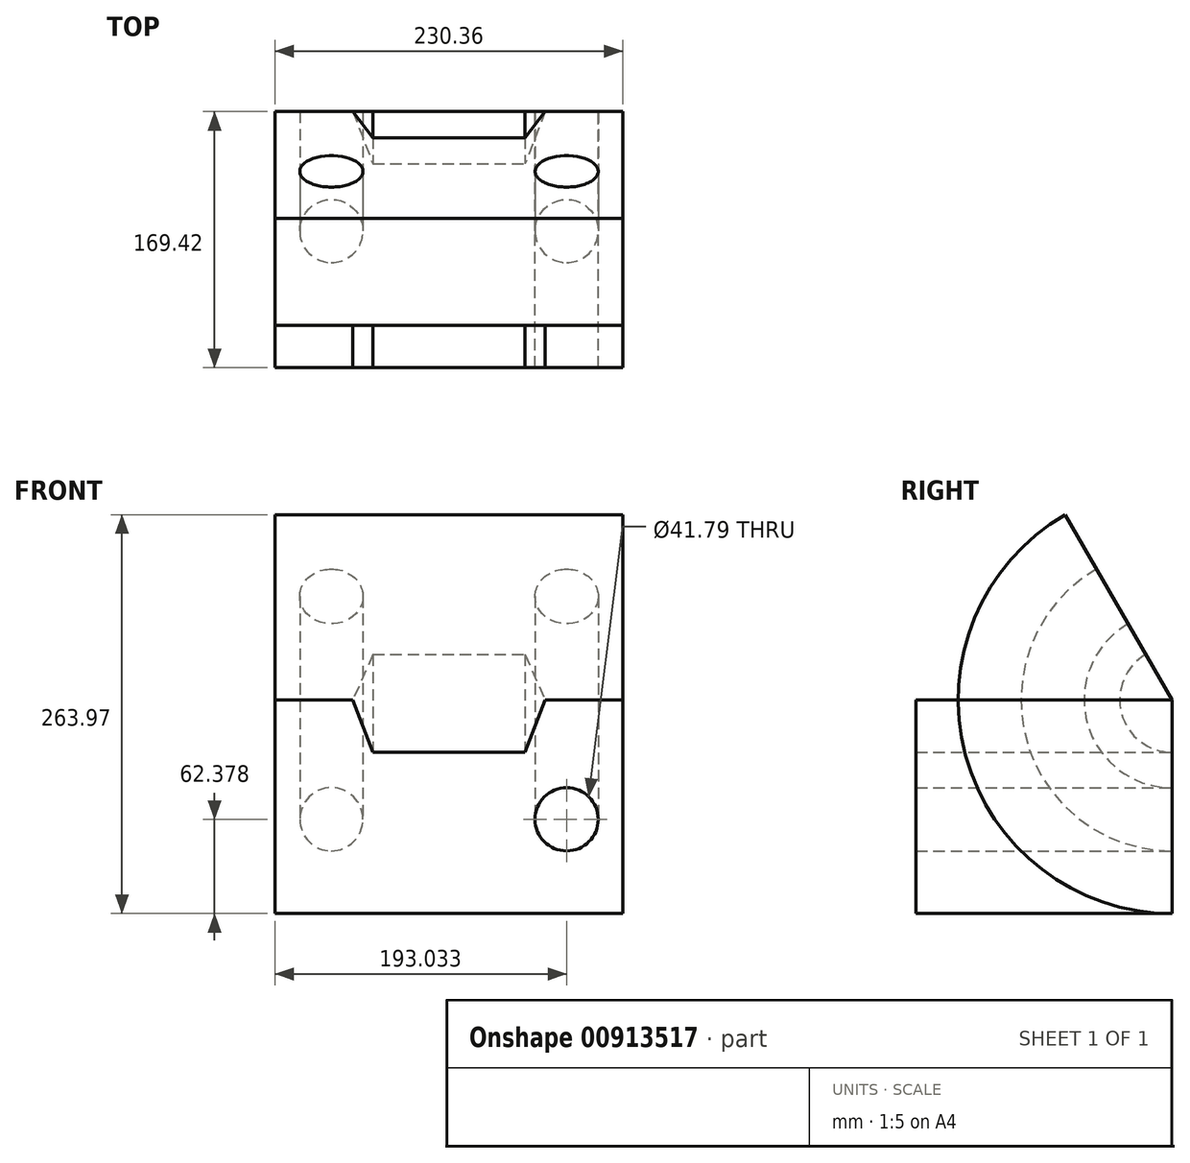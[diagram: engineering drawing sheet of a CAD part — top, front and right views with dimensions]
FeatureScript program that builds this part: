
annotation { "Feature Type Name" : "Feature", "Feature Type Description" : "" }
export const myFeature = defineFeature(function(context is Context, id is Id, definition is map)
    precondition{}
    {
        {
            var Q0;
            Q0=qCreatedBy(makeId("Front.planeOp"),FACE);
            var sketch = newSketch(context, id + "F0", { "sketchPlane" : qUnion([Q0])});
            skLineSegment(sketch, "E0", {"start": v(0, 0) * mm, "end": v(50.35, 0) * mm});
            skLineSegment(sketch, "E1", {"start": v(50.35, 0) * mm, "end": v(63.6, 34.63) * mm});
            skLineSegment(sketch, "E2", {"start": v(63.6, 34.63) * mm, "end": v(115.18, 34.63) * mm});
            skLineSegment(sketch, "E3", {"start": v(115.18, 34.63) * mm, "end": v(115.18, 0) * mm});
            skLineSegment(sketch, "E4", {"start": v(115.18, 0) * mm, "end": v(115.18, -106.83) * mm});
            skLineSegment(sketch, "E5", {"start": v(115.18, -106.83) * mm, "end": v(0, -106.83) * mm});
            skLineSegment(sketch, "E6", {"start": v(0, 74.41) * mm, "end": v(0, -125.5) * mm, "construction": true});
            skLineSegment(sketch, "E7.MirrorCS", {"start": v(-50.35, 0) * mm, "end": v(-63.6, 34.63) * mm});
            skLineSegment(sketch, "E8.MirrorCS", {"start": v(-63.6, 34.63) * mm, "end": v(-115.18, 34.63) * mm});
            skLineSegment(sketch, "E9.MirrorCS", {"start": v(-115.18, -106.83) * mm, "end": v(0, -106.83) * mm});
            skLineSegment(sketch, "E10.MirrorCS", {"start": v(-115.18, 34.63) * mm, "end": v(-115.18, 0) * mm});
            skLineSegment(sketch, "E11.MirrorCS", {"start": v(-115.18, 0) * mm, "end": v(-115.18, -106.83) * mm});
            skLineSegment(sketch, "E12.MirrorCS", {"start": v(0, 0) * mm, "end": v(-50.35, 0) * mm});
            skCircle(sketch, "E13", {"center": v(-77.85, -44.45) * mm, "radius": 20.9 * mm});
            skCircle(sketch, "E14.MirrorC", {"center": v(77.85, -44.45) * mm, "radius": 20.9 * mm});
            skSolve(sketch);
        }
        {
            var Q0;
            Q0=makeQuery(id+"F0.imprint","IMPRINT",FACE,{"disambiguationData":[TD([[makeQuery(id+"F0.imprint","IMPRINT",EDGE,{"derivedFrom":sQuery(id+"F0.wireOp",EDGE,"E0")}),-1.0]])]});
            extrude(context, id + "F1", {"entities" : qUnion([Q0]), "depth" : 111.25 * mm, "offsetDistance" : 25.4 * mm});
        }
        {
            var Q0;
            Q0=makeQuery(id+"F0.imprint","IMPRINT",FACE,{"disambiguationData":[TD([[makeQuery(id+"F0.imprint","IMPRINT",EDGE,{"derivedFrom":sQuery(id+"F0.wireOp",EDGE,"E14.MirrorC")}),-1.0]])]});
            var Q1;
            Q1=makeQuery(id+"F0.imprint","IMPRINT",FACE,{"disambiguationData":[TD([[makeQuery(id+"F0.imprint","IMPRINT",EDGE,{"derivedFrom":sQuery(id+"F0.wireOp",EDGE,"E13")}),1.0]])]});
            extrude(context, id + "F2", {"entities" : qUnion([Q0, Q1]), "operationType" : NewBodyOperationType.ADD, "depth" : 169.42 * mm, "offsetDistance" : 25.4 * mm});
        }
        {
            var Q0;
            Q0=makeQuery(id+"F0.imprint","IMPRINT",FACE,{"disambiguationData":[TD([[makeQuery(id+"F0.imprint","IMPRINT",EDGE,{"derivedFrom":sQuery(id+"F0.wireOp",EDGE,"E0")}),-1.0]])]});
            var Q1;
            Q1=sQuery(id+"F0.wireOp",EDGE,"E2");
            revolve(context, id + "F3", {"surfaceOperationType" : NewSurfaceOperationType.NEW, "entities" : qUnion([Q0]), "axis" : qUnion([Q1]), "revolveType" : RevolveType.ONE_DIRECTION, "oppositeDirection" : true, "angle" : 150 * degree});
        }
    });
